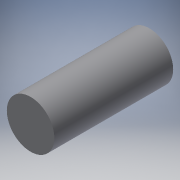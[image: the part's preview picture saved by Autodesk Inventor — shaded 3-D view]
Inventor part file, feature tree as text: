
AUTODESK INVENTOR PART (.ipt)
format: ipt  version: 2018.1 (Build 221171000, 171)  size: 90,624 bytes
history: native  units: mm
features: extrude x1, sketch x1
ambient origin geometry x8: Origin, YZ Plane, XZ Plane, XY Plane, X Axis, Y Axis, Z Axis, Center Point
bodies: Solid1 (feature_tree)
feature tree (2):
  extrude  "Extrusion1"  Depth=50.0mm TaperAngle=0.0deg
  sketch  "Sketch1"  dims[d0=20.0mm d1=50.0mm d2=0.0mm]
